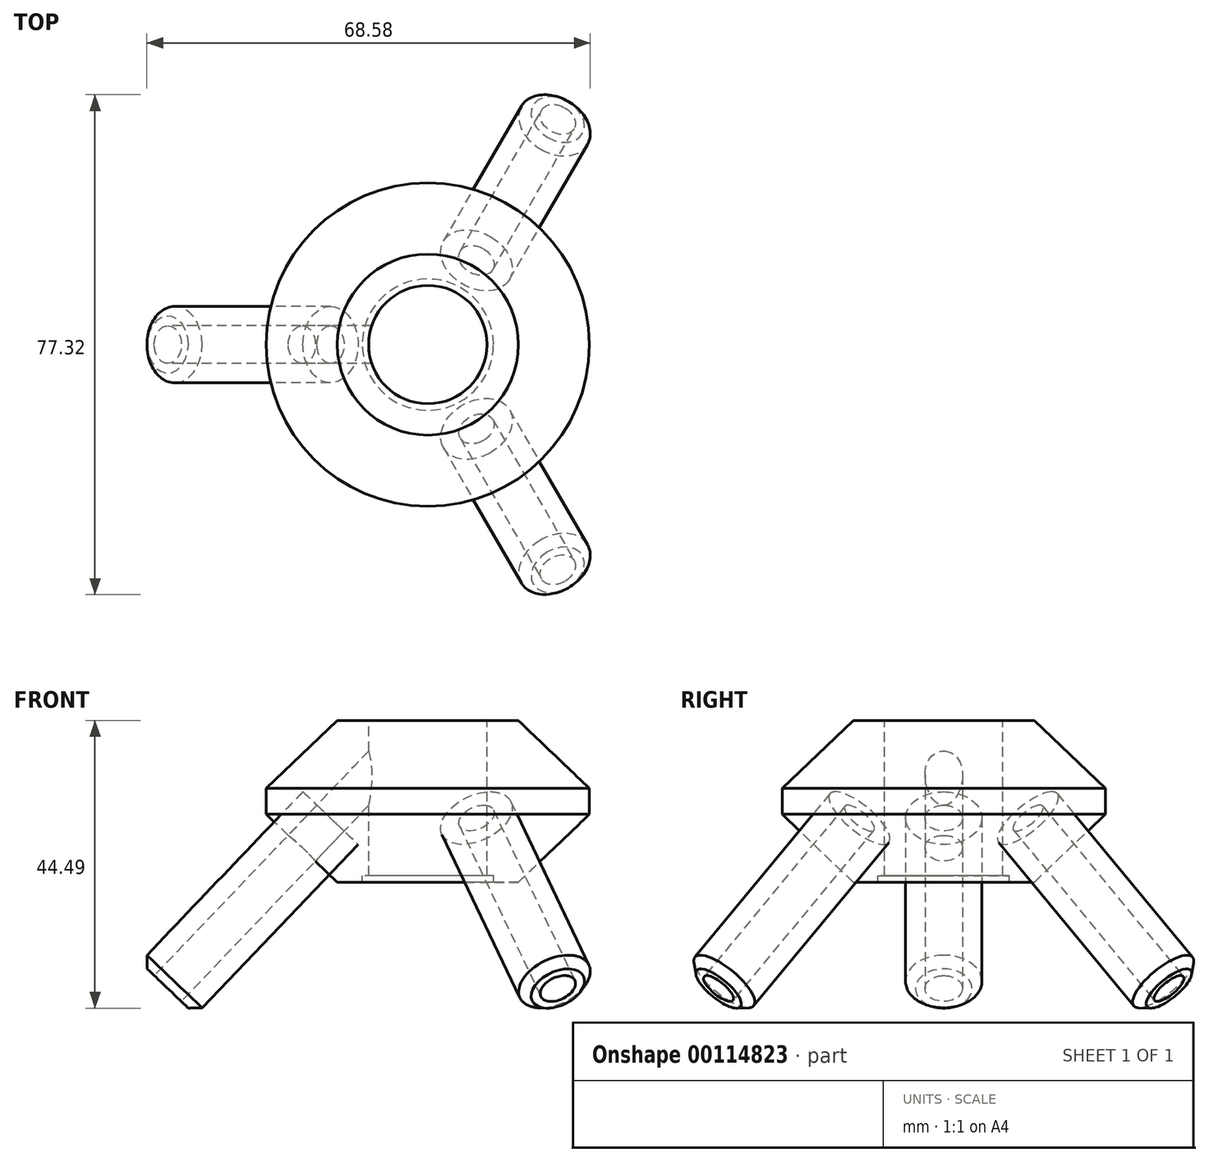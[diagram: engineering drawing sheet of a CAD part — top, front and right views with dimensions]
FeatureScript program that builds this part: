
annotation { "Feature Type Name" : "Feature", "Feature Type Description" : "" }
export const myFeature = defineFeature(function(context is Context, id is Id, definition is map)
    precondition{}
    {
        {
            var Q0;
            Q0=qCreatedBy(makeId("Front.planeOp"),FACE);
            var sketch = newSketch(context, id + "F0", { "sketchPlane" : qUnion([Q0])});
            skLineSegment(sketch, "E0", {"start": v(-9.15, 25) * mm, "end": v(-14, 25) * mm});
            skLineSegment(sketch, "E1", {"start": v(-14, 25) * mm, "end": v(-25, 14.5) * mm});
            skLineSegment(sketch, "E2", {"start": v(-25, 14.5) * mm, "end": v(-25, 10.5) * mm});
            skLineSegment(sketch, "E3", {"start": v(-25, 10.5) * mm, "end": v(-14, 0) * mm});
            skPoint(sketch, "E4.end.orphan", {"position": v(0, 65) * mm});
            skLineSegment(sketch, "E5", {"start": v(-9.15, 25) * mm, "end": v(-9.15, 1) * mm});
            skPoint(sketch, "E6.orphan", {"position": v(0, 25) * mm});
            skLineSegment(sketch, "E7", {"start": v(-14, 0) * mm, "end": v(-10.15, 0) * mm});
            skLineSegment(sketch, "E8", {"start": v(-10.15, 0) * mm, "end": v(-10.15, 1) * mm});
            skLineSegment(sketch, "E9", {"start": v(-10.15, 1) * mm, "end": v(-9.15, 1) * mm});
            skLineSegment(sketch, "E10", {"start": v(0, 25) * mm, "end": v(0, 0) * mm, "construction": true});
            skSolve(sketch);
        }
        {
            var Q0;
            Q0=makeQuery(id+"F0.imprint","IMPRINT",FACE,{"disambiguationData":[TD([[makeQuery(id+"F0.imprint","IMPRINT",EDGE,{"derivedFrom":sQuery(id+"F0.wireOp",EDGE,"E0")}),1.0]])]});
            var Q1;
            Q1=sQuery(id+"F0.wireOp",EDGE,"E10");
            revolve(context, id + "F1", {"entities" : qUnion([Q0]), "axis" : qUnion([Q1]), "revolveType" : RevolveType.FULL});
        }
        {
            var Q0;
            Q0=qCreatedBy(makeId("Front.planeOp"),FACE);
            var sketch = newSketch(context, id + "F2", { "sketchPlane" : qUnion([Q0])});
            skLineSegment(sketch, "E11", {"start": v(-15.23, 1.18) * mm, "end": v(-35.95, -20.52) * mm});
            skLineSegment(sketch, "E12", {"start": v(-35.95, -20.52) * mm, "end": v(-40.21, -16.45) * mm});
            skLineSegment(sketch, "E13", {"start": v(-40.21, -16.45) * mm, "end": v(-19.5, 5.25) * mm});
            skLineSegment(sketch, "E14", {"start": v(-19.5, 5.25) * mm, "end": v(-15.05, 9.91) * mm});
            skLineSegment(sketch, "E15", {"start": v(-15.05, 9.91) * mm, "end": v(-10.78, 5.84) * mm});
            skLineSegment(sketch, "E16", {"start": v(-10.78, 5.84) * mm, "end": v(-15.23, 1.18) * mm});
            skSolve(sketch);
        }
        {
            var Q0;
            Q0=qSketchRegion(id+"F2",true);
            var Q1;
            Q1=sQuery(id+"F2.wireOp",EDGE,"E13");
            revolve(context, id + "F3", {"entities" : qUnion([Q0]), "axis" : qUnion([Q1]), "revolveType" : RevolveType.FULL});
        }
        {
            var Q0;
            Q0=makeQuery(id+"F3.opRevolve","SWEPT_FACE",FACE,{"disambiguationData":[OSD([sQuery(id+"F2.wireOp",EDGE,"E12")])]});
            var sketch = newSketch(context, id + "F4", { "sketchPlane" : qUnion([Q0])});
            skCircle(sketch, "E17", {"center": v(-17.73, 0) * mm, "radius": 2.9 * mm});
            skSolve(sketch);
        }
        {
            var Q0;
            Q0=qSketchRegion(id+"F4",true);
            extrude(context, id + "F5", {"entities" : qUnion([Q0]), "operationType" : NewBodyOperationType.REMOVE, "endBound" : BoundingType.THROUGH_ALL, "oppositeDirection" : true, "depth" : 25 * mm});
        }
        {
            var Q0;
            Q0=makeQuery(id+"F3.opRevolve","SWEPT_EDGE",EDGE,{"disambiguationData":[OSD([sQuery(id+"F2.wireOp",EDGE,"E11"),sQuery(id+"F2.wireOp",EDGE,"E12")])]});
            chamfer(context, id + "F6", {"entities" : qUnion([Q0]), "width" : 1.5 * mm, "tangentPropagation" : true});
        }
        {
            var Q0;
            Q0=makeQuery(id+"F3.opRevolve","SWEPT_BODY",BODY,{"disambiguationData":[OSD([sQuery(id+"F2.wireOp",EDGE,"E11"),sQuery(id+"F2.wireOp",EDGE,"E12"),sQuery(id+"F2.wireOp",EDGE,"E13"),sQuery(id+"F2.wireOp",EDGE,"E14"),sQuery(id+"F2.wireOp",EDGE,"E15"),sQuery(id+"F2.wireOp",EDGE,"E16")])]});
            var Q1;
            Q1=makeQuery(id+"F1.opRevolve","SWEPT_FACE",FACE,{"disambiguationData":[OSD([sQuery(id+"F0.wireOp",EDGE,"E2")])]});
            circularPattern(context, id + "F7", {"entities" : qUnion([Q0]), "axis" : qUnion([Q1]), "angle" : 360 * degree, "instanceCount" : 3, "equalSpace" : true});
        }
    });
